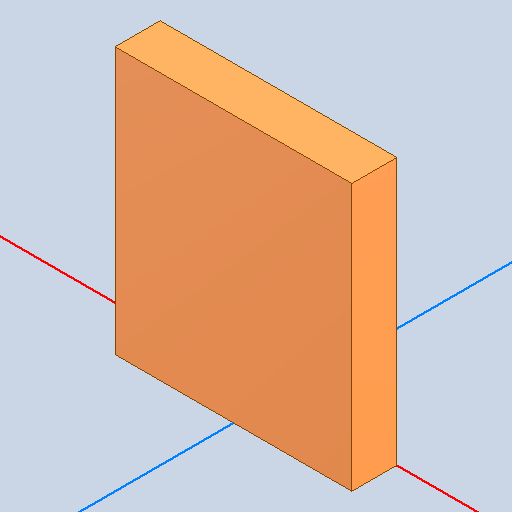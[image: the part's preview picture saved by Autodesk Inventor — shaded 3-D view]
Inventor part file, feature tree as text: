
AUTODESK INVENTOR PART (.ipt)
format: ipt  version: 2022 (Build 260153000, 153)  size: 92,672 bytes
history: native  units: mm
features: other x2, extrude x1
ambient origin geometry x8: Origin, YZ Plane, XZ Plane, XY Plane, X Axis, Y Axis, Z Axis, Center Point
bodies: Body1 (feature_tree)
feature tree (3):
  other  "Твердое тело1"
  extrude  "Выдавливание1"  Depth=1.0mm TaperAngle=0.0deg
  other  "LED5MM, LED5MM_21"
